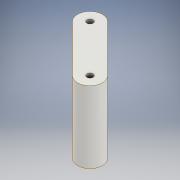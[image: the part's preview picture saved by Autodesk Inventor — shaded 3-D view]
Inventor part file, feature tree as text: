
AUTODESK INVENTOR PART (.ipt)
format: ipt  version: 2020 (Build 240168000, 168)  size: 410,624 bytes
history: native  units: mm
features: projected_geometry x11, other x4, extrude x2, sketch x2, fillet x1
ambient origin geometry x8: Origin, YZ Plane, XZ Plane, XY Plane, X Axis, Y Axis, Z Axis, Center Point
bodies: Body1 (feature_tree)
feature tree (20):
  other  "motor_converter.ipt"
  extrude  "Выдавливание1"  Depth=10.0mm
  extrude  "Выдавливание2"  TaperAngle=0.0deg  [1 undecoded]
  fillet  "Сопряжение1"  Radius=6.0mm
  other  "Твердое тело7::motor_converter.ipt"
  other  "Элемент создания тегов1"
  sketch  "Эскиз1"
  projected_geometry  "Спроецированная петля1"
  projected_geometry  "Спроецированная петля2"
  projected_geometry  "Спроецированная петля3"
  projected_geometry  "Спроецированная петля4"
  projected_geometry  "Спроецированная петля5"
  projected_geometry  "Спроецированная петля6"
  projected_geometry  "Спроецированная петля7"
  projected_geometry  "Спроецированная петля8"
  projected_geometry  "Спроецированная петля9"
  projected_geometry  "Спроецированная петля10"
  sketch  "Эскиз2"
  projected_geometry  "Спроецированная петля11"
  other  "Твердое тело1"
note: 1 required parameter value undecoded (feature->parameter linkage not recoverable at this tier; creation-order binding heuristic only, values carry confidence <= 0.55)
